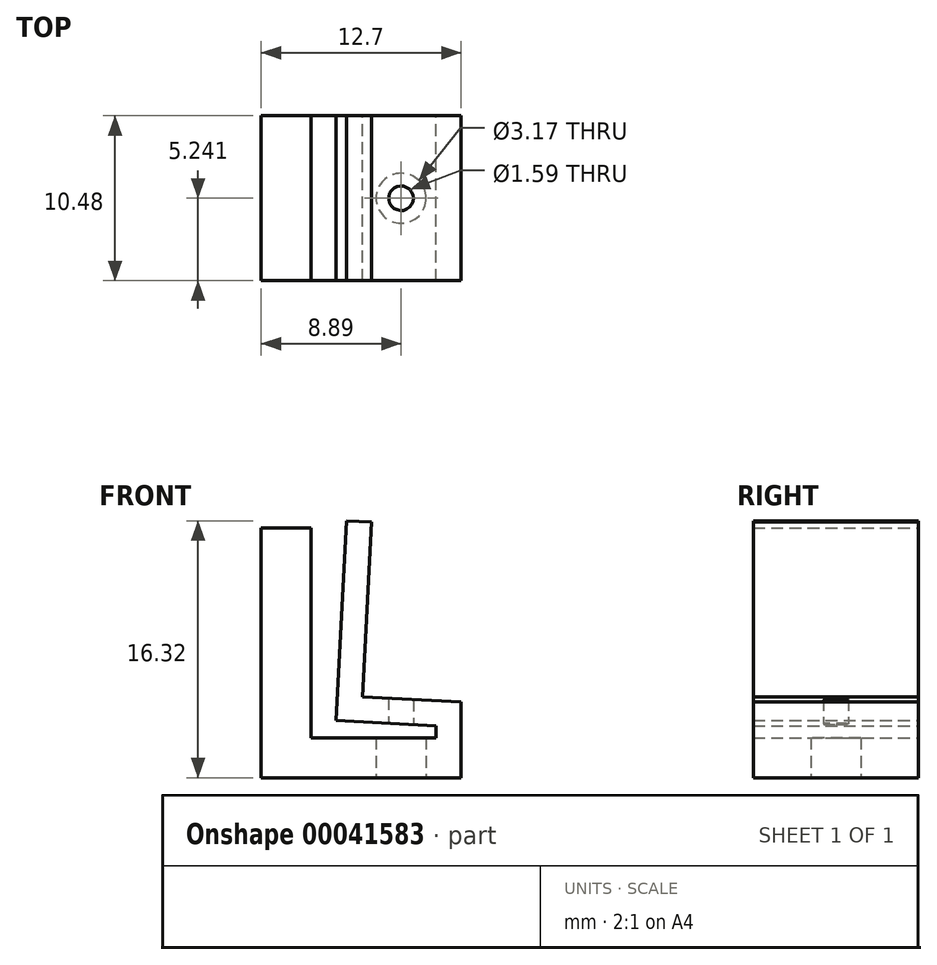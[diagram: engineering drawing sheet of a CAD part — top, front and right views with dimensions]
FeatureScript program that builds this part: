
annotation { "Feature Type Name" : "Feature", "Feature Type Description" : "" }
export const myFeature = defineFeature(function(context is Context, id is Id, definition is map)
    precondition{}
    {
        {
            var Q0;
            Q0=qCreatedBy(makeId("Front.planeOp"),FACE);
            var sketch = newSketch(context, id + "F0", { "sketchPlane" : qUnion([Q0])});
            skLineSegment(sketch, "E0", {"start": v(0, 15.87) * mm, "end": v(0, 0) * mm});
            skLineSegment(sketch, "E1", {"start": v(0, 0) * mm, "end": v(12.7, 0) * mm});
            skLineSegment(sketch, "E2", {"start": v(11.11, 2.54) * mm, "end": v(3.18, 2.54) * mm});
            skLineSegment(sketch, "E3", {"start": v(3.18, 2.54) * mm, "end": v(3.18, 15.88) * mm});
            skLineSegment(sketch, "E4", {"start": v(3.18, 15.88) * mm, "end": v(0, 15.88) * mm});
            skLineSegment(sketch, "E5", {"start": v(12.7, 0) * mm, "end": v(12.7, 4.8) * mm});
            skLineSegment(sketch, "E6", {"start": v(12.7, 4.8) * mm, "end": v(6.43, 5.14) * mm});
            skLineSegment(sketch, "E7", {"start": v(6.43, 5.14) * mm, "end": v(7.01, 16.23) * mm});
            skLineSegment(sketch, "E8", {"start": v(7.01, 16.23) * mm, "end": v(5.43, 16.32) * mm});
            skLineSegment(sketch, "E9", {"start": v(5.43, 16.32) * mm, "end": v(4.76, 3.63) * mm});
            skLineSegment(sketch, "E10", {"start": v(4.76, 3.63) * mm, "end": v(11.11, 3.3) * mm});
            skLineSegment(sketch, "E11", {"start": v(11.11, 3.3) * mm, "end": v(11.11, 2.54) * mm});
            skSolve(sketch);
        }
        {
            var Q0;
            Q0 = qSketchRegion(id + "F0", true);
            extrude(context, id + "F1", {"entities" : qUnion([Q0]), "depth" : 10.48 * mm});
        }
        {
            var Q0;
            Q0=makeQuery(id+"F1.opExtrude","SWEPT_FACE",FACE,{"disambiguationData":[OSD([sQuery(id+"F0.wireOp",EDGE,"E1")])]});
            var sketch = newSketch(context, id + "F2", { "sketchPlane" : qUnion([Q0])});
            skCircle(sketch, "E12", {"center": v(8.9, 5.24) * mm, "radius": 1.59 * mm});
            skLineSegment(sketch, "E13", {"start": v(12.7, 5.24) * mm, "end": v(8.9, 5.24) * mm, "construction": true});
            skSolve(sketch);
        }
        {
            var Q0;
            Q0 = qSketchRegion(id + "F2", true);
            extrude(context, id + "F3", {"entities" : qUnion([Q0]), "operationType" : NewBodyOperationType.REMOVE, "oppositeDirection" : true, "depth" : 2.54 * mm});
        }
        {
            var Q0;
            Q0=makeQuery(id+"F1.opExtrude","SWEPT_FACE",FACE,{"disambiguationData":[OSD([sQuery(id+"F0.wireOp",EDGE,"E1")])]});
            var sketch = newSketch(context, id + "F4", { "sketchPlane" : qUnion([Q0])});
            skCircle(sketch, "E14", {"center": v(8.9, 5.24) * mm, "radius": 0.8 * mm});
            skSolve(sketch);
        }
        {
            var Q0;
            Q0 = qSketchRegion(id + "F4", true);
            extrude(context, id + "F5", {"entities" : qUnion([Q0]), "operationType" : NewBodyOperationType.REMOVE, "endBound" : BoundingType.THROUGH_ALL, "oppositeDirection" : true, "depth" : 25.4 * mm});
        }
    });
